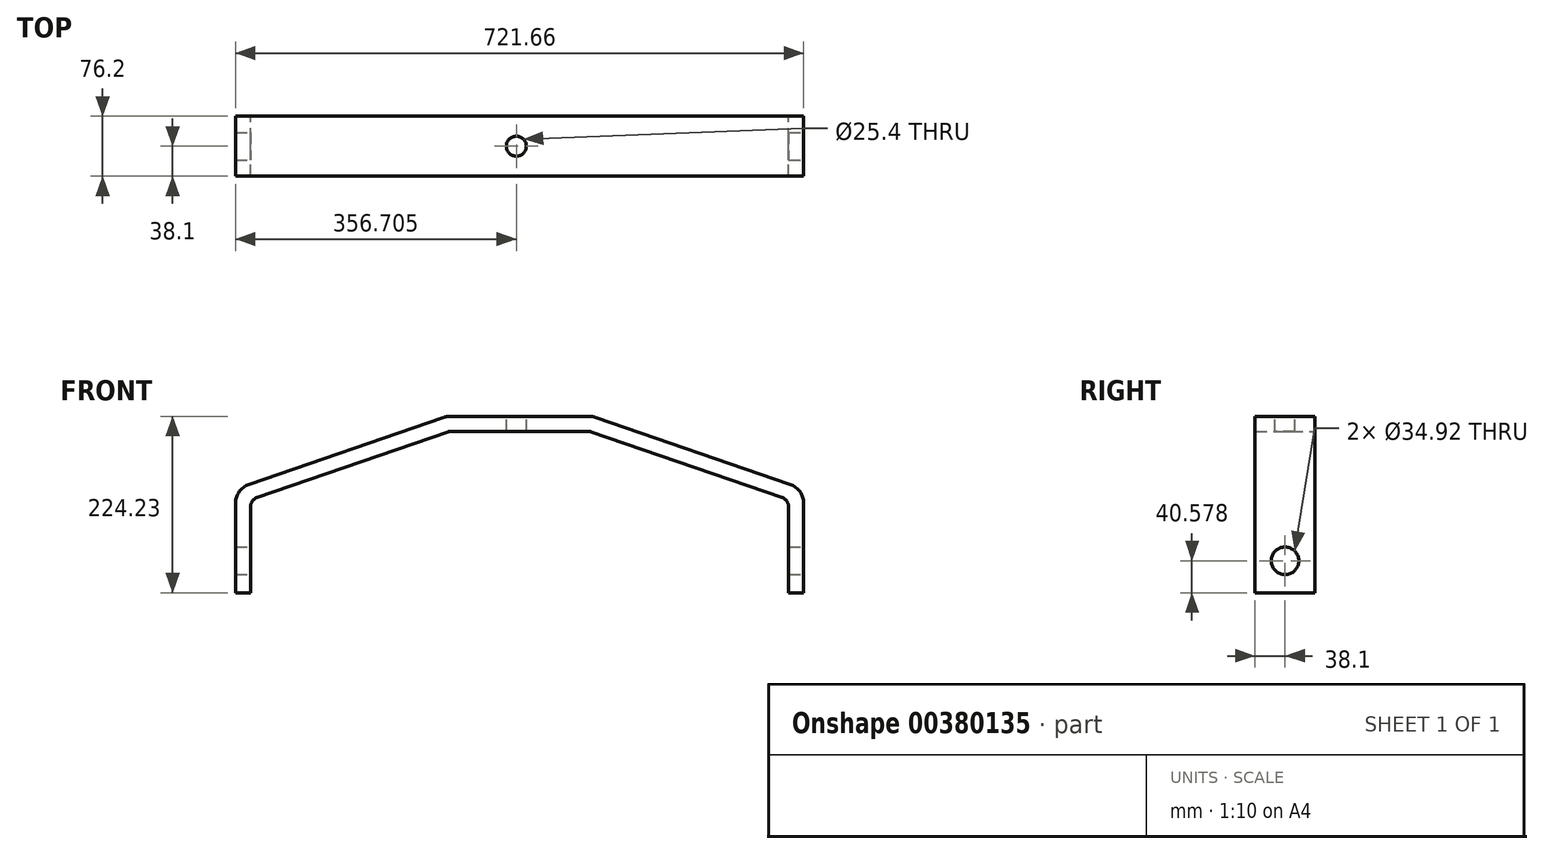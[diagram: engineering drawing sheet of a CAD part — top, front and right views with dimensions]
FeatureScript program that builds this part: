
annotation { "Feature Type Name" : "Feature", "Feature Type Description" : "" }
export const myFeature = defineFeature(function(context is Context, id is Id, definition is map)
    precondition{}
    {
        {
            var Q0;
            Q0=qCreatedBy(makeId("Front.planeOp"),FACE);
            var sketch = newSketch(context, id + "F0", { "sketchPlane" : qUnion([Q0])});
            skLineSegment(sketch, "E0", {"start": v(-45.62, 205.2) * mm, "end": v(132.41, 205.2) * mm});
            skLineSegment(sketch, "E1", {"start": v(132.41, 205.2) * mm, "end": v(385.17, 118.17) * mm});
            skLineSegment(sketch, "E2", {"start": v(385.17, 118.17) * mm, "end": v(385.17, 0.02) * mm});
            skLineSegment(sketch, "E3", {"start": v(-45.62, 205.2) * mm, "end": v(-298.39, 118.17) * mm});
            skLineSegment(sketch, "E4", {"start": v(-298.39, 118.17) * mm, "end": v(-298.39, 0.02) * mm});
            skLineSegment(sketch, "E5.0", {"start": v(-317.44, 131.75) * mm, "end": v(-317.44, 0.02) * mm});
            skLineSegment(sketch, "E5.1", {"start": v(404.22, 131.76) * mm, "end": v(404.22, 0.02) * mm});
            skLineSegment(sketch, "E5.2", {"start": v(135.6, 224.25) * mm, "end": v(404.22, 131.76) * mm});
            skLineSegment(sketch, "E5.3", {"start": v(-48.8, 224.25) * mm, "end": v(135.6, 224.25) * mm});
            skLineSegment(sketch, "E5.4", {"start": v(-48.8, 224.25) * mm, "end": v(-317.44, 131.75) * mm});
            skLineSegment(sketch, "E6", {"start": v(-317.44, 0.02) * mm, "end": v(-298.39, 0.02) * mm});
            skLineSegment(sketch, "E7", {"start": v(385.17, 0.02) * mm, "end": v(404.22, 0.02) * mm});
            skSolve(sketch);
        }
        {
            var Q0;
            Q0 = qSketchRegion(id + "F0", true);
            extrude(context, id + "F1", {"entities" : qUnion([Q0]), "depth" : 76.2 * mm, "symmetric" : true});
        }
        {
            var Q0;
            Q0=makeQuery(id+"F1.opExtrude","SWEPT_EDGE",EDGE,{"disambiguationData":[OSD([sQuery(id+"F0.wireOp",EDGE,"E3"),sQuery(id+"F0.wireOp",EDGE,"E4")])]});
            var Q1;
            Q1=makeQuery(id+"F1.opExtrude","SWEPT_EDGE",EDGE,{"disambiguationData":[OSD([sQuery(id+"F0.wireOp",EDGE,"E0"),sQuery(id+"F0.wireOp",EDGE,"E3")])]});
            var Q2;
            Q2=makeQuery(id+"F1.opExtrude","SWEPT_EDGE",EDGE,{"disambiguationData":[OSD([sQuery(id+"F0.wireOp",EDGE,"E0"),sQuery(id+"F0.wireOp",EDGE,"E1")])]});
            var Q3;
            Q3=makeQuery(id+"F1.opExtrude","SWEPT_EDGE",EDGE,{"disambiguationData":[OSD([sQuery(id+"F0.wireOp",EDGE,"E1"),sQuery(id+"F0.wireOp",EDGE,"E2")])]});
            fillet(context, id + "F2", {"entities" : qUnion([Q0, Q1, Q2, Q3]), "radius" : 12.7 * mm, "tangentPropagation" : true, "allowEdgeOverflow" : false});
        }
        {
            var Q0;
            Q0=makeQuery(id+"F1.opExtrude","SWEPT_EDGE",EDGE,{"disambiguationData":[OSD([sQuery(id+"F0.wireOp",EDGE,"E5.0"),sQuery(id+"F0.wireOp",EDGE,"E5.4")])]});
            var Q1;
            Q1=makeQuery(id+"F1.opExtrude","SWEPT_EDGE",EDGE,{"disambiguationData":[OSD([sQuery(id+"F0.wireOp",EDGE,"E5.3"),sQuery(id+"F0.wireOp",EDGE,"E5.4")])]});
            var Q2;
            Q2=makeQuery(id+"F1.opExtrude","SWEPT_EDGE",EDGE,{"disambiguationData":[OSD([sQuery(id+"F0.wireOp",EDGE,"E5.2"),sQuery(id+"F0.wireOp",EDGE,"E5.3")])]});
            var Q3;
            Q3=makeQuery(id+"F1.opExtrude","SWEPT_EDGE",EDGE,{"disambiguationData":[OSD([sQuery(id+"F0.wireOp",EDGE,"E5.1"),sQuery(id+"F0.wireOp",EDGE,"E5.2")])]});
            fillet(context, id + "F3", {"entities" : qUnion([Q0, Q1, Q2, Q3]), "radius" : 25.4 * mm, "tangentPropagation" : true, "allowEdgeOverflow" : false});
        }
        {
            var Q0;
            Q0=makeQuery(id+"F1.opExtrude","SWEPT_FACE",FACE,{"disambiguationData":[OSD([sQuery(id+"F0.wireOp",EDGE,"E5.1")])]});
            var sketch = newSketch(context, id + "F4", { "sketchPlane" : qUnion([Q0])});
            skCircle(sketch, "E8", {"center": v(0, 40.6) * mm, "radius": 17.46 * mm});
            skSolve(sketch);
        }
        {
            var Q0;
            Q0 = qSketchRegion(id + "F4", true);
            extrude(context, id + "F5", {"entities" : qUnion([Q0]), "operationType" : NewBodyOperationType.REMOVE, "endBound" : BoundingType.THROUGH_ALL, "oppositeDirection" : true, "depth" : 25.4 * mm});
        }
        {
            var Q0;
            Q0=makeQuery(id+"F1.opExtrude","SWEPT_FACE",FACE,{"disambiguationData":[OSD([sQuery(id+"F0.wireOp",EDGE,"E5.3")])]});
            var sketch = newSketch(context, id + "F6", { "sketchPlane" : qUnion([Q0])});
            skCircle(sketch, "E9", {"center": v(39.27, 0) * mm, "radius": 12.7 * mm});
            skSolve(sketch);
        }
        {
            var Q0;
            Q0 = qSketchRegion(id + "F6", true);
            extrude(context, id + "F7", {"entities" : qUnion([Q0]), "operationType" : NewBodyOperationType.REMOVE, "endBound" : BoundingType.THROUGH_ALL, "oppositeDirection" : true, "depth" : 25.4 * mm});
        }
    });
